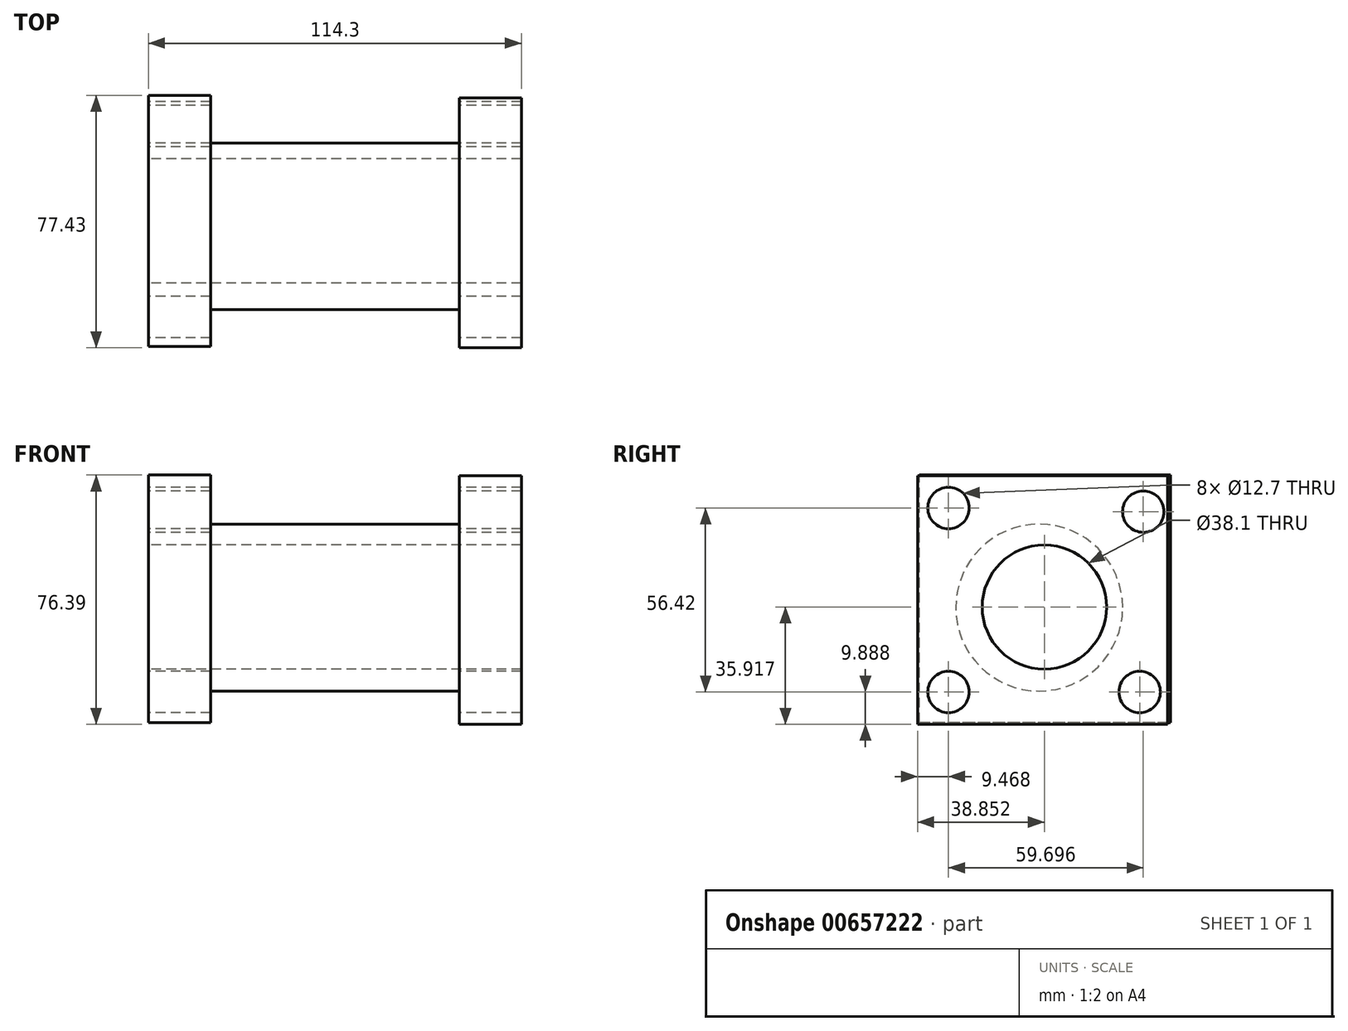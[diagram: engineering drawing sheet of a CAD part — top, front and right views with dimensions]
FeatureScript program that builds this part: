
annotation { "Feature Type Name" : "Feature", "Feature Type Description" : "" }
export const myFeature = defineFeature(function(context is Context, id is Id, definition is map)
    precondition{}
    {
        {
            var Q0;
            Q0=qCreatedBy(makeId("Right.planeOp"),FACE);
            var sketch = newSketch(context, id + "F0", { "sketchPlane" : qUnion([Q0])});
            skLineSegment(sketch, "E0.bottom", {"start": v(-45.03, 48.25) * mm, "end": v(31.57, 48.25) * mm});
            skLineSegment(sketch, "E0.top", {"start": v(-45.03, -27.97) * mm, "end": v(31.57, -27.97) * mm});
            skLineSegment(sketch, "E0.left", {"start": v(-45.03, 48.25) * mm, "end": v(-45.03, -27.97) * mm});
            skLineSegment(sketch, "E0.right", {"start": v(31.57, 48.25) * mm, "end": v(31.57, -27.97) * mm});
            skSolve(sketch);
        }
        {
            var Q0;
            Q0 = qSketchRegion(id + "F0", true);
            extrude(context, id + "F1", {"entities" : qUnion([Q0]), "depth" : 19.05 * mm, "offsetDistance" : 25.4 * mm});
        }
        {
            var Q0;
            Q0=makeQuery(id+"F1.opExtrude","CAP_FACE",FACE,{"disambiguationData":[OSD([sQuery(id+"F0.wireOp",EDGE,"E0.bottom"),sQuery(id+"F0.wireOp",EDGE,"E0.top"),sQuery(id+"F0.wireOp",EDGE,"E0.left"),sQuery(id+"F0.wireOp",EDGE,"E0.right")])],"isStart":true});
            var sketch = newSketch(context, id + "F2", { "sketchPlane" : qUnion([Q0])});
            skCircle(sketch, "E1", {"center": v(7.77, 7.78) * mm, "radius": 25.57 * mm});
            skSolve(sketch);
        }
        {
            var Q0;
            Q0 = qSketchRegion(id + "F2", true);
            extrude(context, id + "F3", {"entities" : qUnion([Q0]), "operationType" : NewBodyOperationType.ADD, "depth" : 76.2 * mm, "offsetDistance" : 25.4 * mm});
        }
        {
            var Q0;
            Q0=makeQuery(id+"F3.opExtrude","CAP_FACE",FACE,{"disambiguationData":[OSD([sQuery(id+"F2.wireOp",EDGE,"E1")])],"isStart":false});
            var sketch = newSketch(context, id + "F4", { "sketchPlane" : qUnion([Q0])});
            skLineSegment(sketch, "E2.bottom", {"start": v(-32.4, -27.43) * mm, "end": v(44.55, -27.43) * mm});
            skLineSegment(sketch, "E2.top", {"start": v(-32.4, 48.42) * mm, "end": v(44.55, 48.42) * mm});
            skLineSegment(sketch, "E2.left", {"start": v(-32.4, -27.43) * mm, "end": v(-32.4, 48.42) * mm});
            skLineSegment(sketch, "E2.right", {"start": v(44.55, -27.43) * mm, "end": v(44.55, 48.42) * mm});
            skSolve(sketch);
        }
        {
            var Q0;
            Q0 = qSketchRegion(id + "F4", true);
            extrude(context, id + "F5", {"entities" : qUnion([Q0]), "operationType" : NewBodyOperationType.ADD, "depth" : 19.05 * mm, "offsetDistance" : 25.4 * mm});
        }
        {
            var Q0;
            Q0=makeQuery(id+"F5.opExtrude","CAP_FACE",FACE,{"disambiguationData":[OSD([sQuery(id+"F4.wireOp",EDGE,"E2.bottom"),sQuery(id+"F4.wireOp",EDGE,"E2.top"),sQuery(id+"F4.wireOp",EDGE,"E2.left"),sQuery(id+"F4.wireOp",EDGE,"E2.right")])],"isStart":false});
            var sketch = newSketch(context, id + "F6", { "sketchPlane" : qUnion([Q0])});
            skCircle(sketch, "E3", {"center": v(6.18, 7.95) * mm, "radius": 19.07 * mm});
            skSolve(sketch);
        }
        {
            var Q0;
            Q0=makeQuery(id+"F6.imprint","IMPRINT",FACE,{"disambiguationData":[TD([[makeQuery(id+"F6.imprint","IMPRINT",EDGE,{"derivedFrom":sQuery(id+"F6.wireOp",EDGE,"E3")}),-1.0]])]});
            var sketch = newSketch(context, id + "F7", { "sketchPlane" : qUnion([Q0])});
            skCircle(sketch, "E4", {"center": v(-23.01, -18.08) * mm, "radius": 6.4 * mm});
            skCircle(sketch, "E5", {"center": v(-24.13, 37.2) * mm, "radius": 6.45 * mm});
            skCircle(sketch, "E6", {"center": v(35.56, -18.08) * mm, "radius": 6.37 * mm});
            skCircle(sketch, "E7", {"center": v(35.56, 38.34) * mm, "radius": 6.35 * mm});
            skSolve(sketch);
        }
        {
            var Q0;
            Q0=sQuery(id+"F7.wireOp",VERTEX,"E4.center");
            var Q1;
            Q1=sQuery(id+"F7.wireOp",VERTEX,"E5.center");
            var Q2;
            Q2=sQuery(id+"F7.wireOp",VERTEX,"E7.center");
            var Q3;
            Q3=sQuery(id+"F7.wireOp",VERTEX,"E6.center");
            var Q4;
            Q4=makeQuery(id+"F1.opExtrude","SWEPT_BODY",BODY,{"disambiguationData":[OSD([sQuery(id+"F0.wireOp",EDGE,"E0.bottom"),sQuery(id+"F0.wireOp",EDGE,"E0.top"),sQuery(id+"F0.wireOp",EDGE,"E0.left"),sQuery(id+"F0.wireOp",EDGE,"E0.right")])]});
            hole(context, id + "F8", {"style" : HoleStyle.SIMPLE, "endStyle" : HoleEndStyle.THROUGH, "holeDiameter" : 12.7 * mm, "majorDiameter" : 6.35 * mm, "isTappedThrough" : true, "tappedDepth" : 12.7 * mm, "tapClearance" : 3, "locations" : qUnion([Q0, Q1, Q2, Q3]), "scope" : qUnion([Q4])});
        }
        {
            var Q0;
            Q0=sQuery(id+"F6.wireOp",VERTEX,"E3.center");
            var Q1;
            Q1=makeQuery(id+"F1.opExtrude","SWEPT_BODY",BODY,{"disambiguationData":[OSD([sQuery(id+"F0.wireOp",EDGE,"E0.bottom"),sQuery(id+"F0.wireOp",EDGE,"E0.top"),sQuery(id+"F0.wireOp",EDGE,"E0.left"),sQuery(id+"F0.wireOp",EDGE,"E0.right")])]});
            hole(context, id + "F9", {"style" : HoleStyle.SIMPLE, "endStyle" : HoleEndStyle.THROUGH, "holeDiameter" : 38.1 * mm, "majorDiameter" : 6.35 * mm, "isTappedThrough" : true, "tappedDepth" : 12.7 * mm, "tapClearance" : 3, "locations" : qUnion([Q0]), "scope" : qUnion([Q1])});
        }
    });
